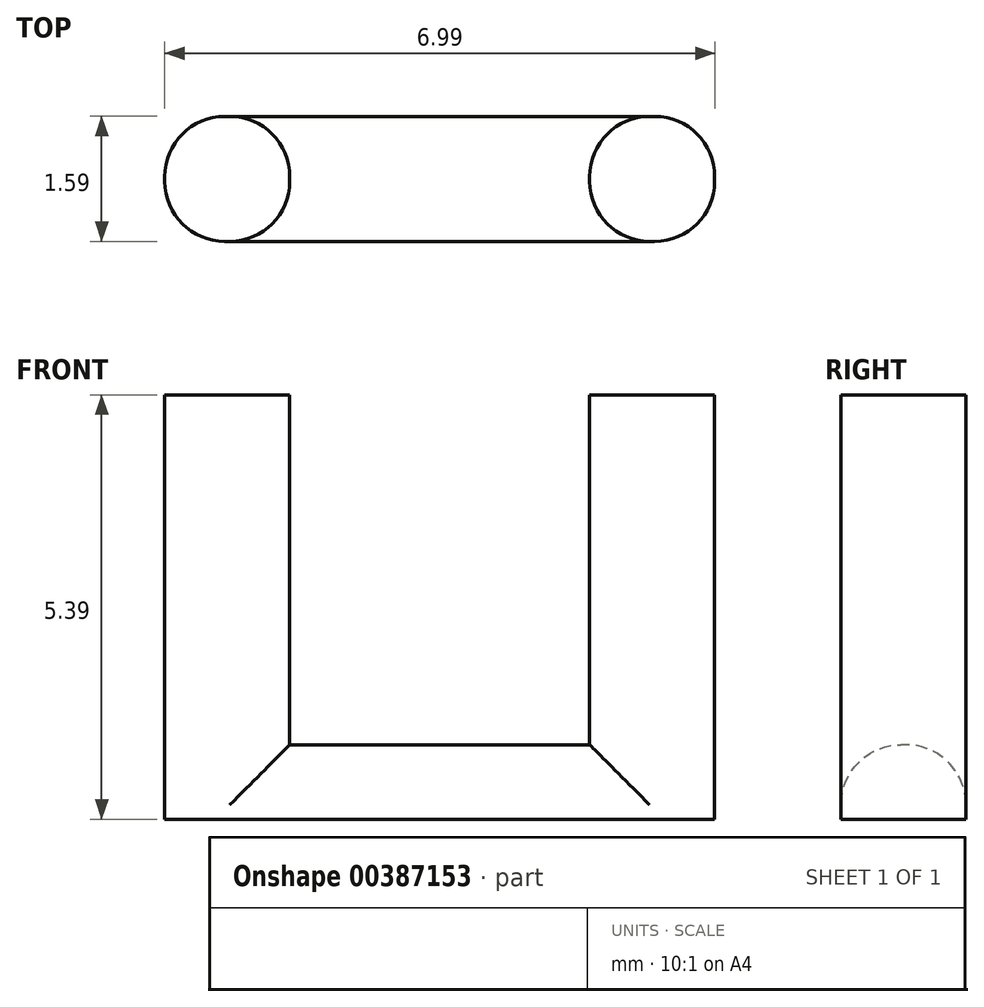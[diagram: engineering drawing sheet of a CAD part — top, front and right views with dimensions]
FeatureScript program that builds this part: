
annotation { "Feature Type Name" : "Feature", "Feature Type Description" : "" }
export const myFeature = defineFeature(function(context is Context, id is Id, definition is map)
    precondition{}
    {
        {
            var Q0;
            Q0=qCreatedBy(makeId("Top.planeOp"),FACE);
            var sketch = newSketch(context, id + "F0", { "sketchPlane" : qUnion([Q0])});
            skLineSegment(sketch, "E0.bottom", {"start": v(0, 0) * mm, "end": v(6.99, 0) * mm});
            skLineSegment(sketch, "E0.top", {"start": v(0, 1.59) * mm, "end": v(6.99, 1.59) * mm});
            skLineSegment(sketch, "E0.left", {"start": v(0, 0) * mm, "end": v(0, 1.59) * mm});
            skLineSegment(sketch, "E0.right", {"start": v(6.99, 0) * mm, "end": v(6.99, 1.59) * mm});
            skSolve(sketch);
        }
        {
            var Q0;
            Q0=qSketchRegion(id+"F0",true);
            extrude(context, id + "F1", {"entities" : qUnion([Q0]), "depth" : 0.95 * mm});
        }
        {
            var Q0;
            Q0=makeQuery(id+"F1.opExtrude","CAP_FACE",FACE,{"disambiguationData":[OSD([sQuery(id+"F0.wireOp",EDGE,"E0.bottom"),sQuery(id+"F0.wireOp",EDGE,"E0.top"),sQuery(id+"F0.wireOp",EDGE,"E0.left"),sQuery(id+"F0.wireOp",EDGE,"E0.right")])],"isStart":false});
            var sketch = newSketch(context, id + "F2", { "sketchPlane" : qUnion([Q0])});
            skLineSegment(sketch, "E1.bottom", {"start": v(0, 1.59) * mm, "end": v(1.59, 1.59) * mm});
            skLineSegment(sketch, "E1.top", {"start": v(0, 0) * mm, "end": v(1.59, 0) * mm});
            skLineSegment(sketch, "E1.left", {"start": v(0, 1.59) * mm, "end": v(0, 0) * mm});
            skLineSegment(sketch, "E1.right", {"start": v(1.59, 1.59) * mm, "end": v(1.59, 0) * mm});
            skLineSegment(sketch, "E2.bottom", {"start": v(6.99, 1.59) * mm, "end": v(5.4, 1.59) * mm});
            skLineSegment(sketch, "E2.top", {"start": v(6.99, 0) * mm, "end": v(5.4, 0) * mm});
            skLineSegment(sketch, "E2.left", {"start": v(6.99, 1.59) * mm, "end": v(6.99, 0) * mm});
            skLineSegment(sketch, "E2.right", {"start": v(5.4, 1.59) * mm, "end": v(5.4, 0) * mm});
            skSolve(sketch);
        }
        {
            var Q0;
            Q0=qSketchRegion(id+"F2",true);
            extrude(context, id + "F3", {"entities" : qUnion([Q0]), "operationType" : NewBodyOperationType.ADD, "depth" : 4.44 * mm});
        }
        {
            var Q0;
            Q0=makeQuery(id+"F3.boolean.opBoolean","MERGE",EDGE,{"derivedFrom":[makeQuery(id+"F1.opExtrude","SWEPT_EDGE",EDGE,{"disambiguationData":[OSD([sQuery(id+"F0.wireOp",EDGE,"E0.bottom"),sQuery(id+"F0.wireOp",EDGE,"E0.left")])]}),makeQuery(id+"F3.opExtrude","SWEPT_EDGE",EDGE,{"disambiguationData":[OSD([sQuery(id+"F2.wireOp",EDGE,"E1.top"),sQuery(id+"F2.wireOp",EDGE,"E1.left")])]})]});
            var Q1;
            Q1=makeQuery(id+"F3.opExtrude","SWEPT_EDGE",EDGE,{"disambiguationData":[OSD([sQuery(id+"F0.wireOp",EDGE,"E0.bottom"),sQuery(id+"F2.wireOp",EDGE,"E1.top"),sQuery(id+"F2.wireOp",EDGE,"E1.right")])]});
            var Q2;
            Q2=makeQuery(id+"F1.opExtrude","CAP_EDGE",EDGE,{"disambiguationData":[OSD([sQuery(id+"F0.wireOp",EDGE,"E0.bottom")])],"isStart":false});
            var Q3;
            Q3=makeQuery(id+"F3.opExtrude","SWEPT_EDGE",EDGE,{"disambiguationData":[OSD([sQuery(id+"F0.wireOp",EDGE,"E0.bottom"),sQuery(id+"F2.wireOp",EDGE,"E2.top"),sQuery(id+"F2.wireOp",EDGE,"E2.right")])]});
            var Q4;
            Q4=makeQuery(id+"F3.boolean.opBoolean","MERGE",EDGE,{"derivedFrom":[makeQuery(id+"F1.opExtrude","SWEPT_EDGE",EDGE,{"disambiguationData":[OSD([sQuery(id+"F0.wireOp",EDGE,"E0.bottom"),sQuery(id+"F0.wireOp",EDGE,"E0.right")])]}),makeQuery(id+"F3.opExtrude","SWEPT_EDGE",EDGE,{"disambiguationData":[OSD([sQuery(id+"F2.wireOp",EDGE,"E2.top"),sQuery(id+"F2.wireOp",EDGE,"E2.left")])]})]});
            var Q5;
            Q5=makeQuery(id+"F3.boolean.opBoolean","MERGE",EDGE,{"derivedFrom":[makeQuery(id+"F1.opExtrude","SWEPT_EDGE",EDGE,{"disambiguationData":[OSD([sQuery(id+"F0.wireOp",EDGE,"E0.top"),sQuery(id+"F0.wireOp",EDGE,"E0.left")])]}),makeQuery(id+"F3.opExtrude","SWEPT_EDGE",EDGE,{"disambiguationData":[OSD([sQuery(id+"F2.wireOp",EDGE,"E1.bottom"),sQuery(id+"F2.wireOp",EDGE,"E1.left")])]})]});
            var Q6;
            Q6=makeQuery(id+"F3.opExtrude","SWEPT_EDGE",EDGE,{"disambiguationData":[OSD([sQuery(id+"F0.wireOp",EDGE,"E0.top"),sQuery(id+"F2.wireOp",EDGE,"E1.bottom"),sQuery(id+"F2.wireOp",EDGE,"E1.right")])]});
            var Q7;
            Q7=makeQuery(id+"F1.opExtrude","CAP_EDGE",EDGE,{"disambiguationData":[OSD([sQuery(id+"F0.wireOp",EDGE,"E0.top")])],"isStart":false});
            var Q8;
            Q8=makeQuery(id+"F3.opExtrude","SWEPT_EDGE",EDGE,{"disambiguationData":[OSD([sQuery(id+"F0.wireOp",EDGE,"E0.top"),sQuery(id+"F2.wireOp",EDGE,"E2.bottom"),sQuery(id+"F2.wireOp",EDGE,"E2.right")])]});
            var Q9;
            Q9=makeQuery(id+"F3.boolean.opBoolean","MERGE",EDGE,{"derivedFrom":[makeQuery(id+"F1.opExtrude","SWEPT_EDGE",EDGE,{"disambiguationData":[OSD([sQuery(id+"F0.wireOp",EDGE,"E0.top"),sQuery(id+"F0.wireOp",EDGE,"E0.right")])]}),makeQuery(id+"F3.opExtrude","SWEPT_EDGE",EDGE,{"disambiguationData":[OSD([sQuery(id+"F2.wireOp",EDGE,"E2.bottom"),sQuery(id+"F2.wireOp",EDGE,"E2.left")])]})]});
            fillet(context, id + "F4", {"entities" : qUnion([Q0, Q1, Q2, Q3, Q4, Q5, Q6, Q7, Q8, Q9]), "radius" : 0.76 * mm, "tangentPropagation" : true, "allowEdgeOverflow" : false});
        }
    });
